FCSTD DOCUMENT  (FreeCAD 0.20R29177 (Git))
Label: Tail_Assembly
License: All rights reserved
LicenseURL: http://en.wikipedia.org/wiki/All_rights_reserved
objects: App::Link×2, Spreadsheet::Sheet×1, App::Part×1
EXTERNAL_REF file=../Master_of_Puppets.FCStd obj=HighEndStop
EXTERNAL_REF file=Hinge/Inner/Tail_Hinge_Inner.FCStd obj=Part001
EXTERNAL_REF file=Tail.FCStd obj=Part

FEATURE [Spreadsheet::Sheet] Spreadsheet
  cells = A1=Inputs; A2=TailAssemblyPlacement; B2(TailAssemblyPlacement)==Master_of_Puppets#HighEndStop.TailAssemblyPlacement
FEATURE [App::Link] Link  label="Hinge_Inner"
  LinkedObject = -> <external Hinge/Inner/Tail_Hinge_Inner.FCStd>#Part001
FEATURE [App::Link] Link001  label="Tail"
  LinkTransform = true
  LinkedObject = -> <external Tail.FCStd>#Part
FEATURE [App::Part] Part  label="Tail_Assembly"
  Group = -> [Link,Link001]
  Origin = -> Origin
  Placement = pos=(-8.64666,-12.3487,0) rot=(0,0,-1;2.18166rad)
  expr: Placement = Spreadsheet.TailAssemblyPlacement

RESOLVED EXTERNAL PARTS (link-assembly join: the EXTERNAL_REF files above that resolve inside this repo's crawl, each included once):
---- part ../Master_of_Puppets.FCStd = doc fcstd_6404554055c4 (61625 chars; too large to inline — full recipe in that document) ----
---- part Hinge/Inner/Tail_Hinge_Inner.FCStd = doc fcstd_5a32ac608b16 ----
FCSTD DOCUMENT  (FreeCAD 1.0R39109 (Git))
Label: Tail_Hinge_Inner
License: All rights reserved
LicenseURL: http://en.wikipedia.org/wiki/All_rights_reserved
objects: App::Link×3, Spreadsheet::Sheet×1, App::Part×1
EXTERNAL_REF file=Tail_Hinge_Inner_Pipe.FCStd obj=Tube
EXTERNAL_REF file=../../../Master_of_Puppets.FCStd obj=Spreadsheet
EXTERNAL_REF file=../../../Master_of_Puppets.FCStd obj=Tail
EXTERNAL_REF file=../Junction/Tail_Hinge_Junction.FCStd obj=Part
EXTERNAL_REF file=Tail_Hinge_Inner_Pipe_Cover.FCStd obj=Cylinder

FEATURE [App::Link] Link  label="Pipe"
  LinkPlacement = pos=(31.9025,0,-7.21663) rot=(0,1,0;0.349066rad)
  LinkedObject = -> <external Tail_Hinge_Inner_Pipe.FCStd>#Tube
  Placement = pos=(31.9025,0,-7.21663) rot=(0,1,0;0.349066rad)
  expr: .LinkPlacement.Base.x = Spreadsheet.TailHingePipeX
  expr: .LinkPlacement.Base.z = Spreadsheet.TailHingePipeZ
  expr: Placement = Spreadsheet.HingeInnerPipePlacement
FEATURE [Spreadsheet::Sheet] Spreadsheet
  cells = A1='Inputs; A2='VerticalPlaneAngle; B2(VerticalPlaneAngle)==Master_of_Puppets#Spreadsheet.VerticalPlaneAngle; A3='HingeInnerPipeRadius; B3(HingeInnerPipeRadius)==Master_of_Puppets#Tail.HingeInnerPipeRadius; A4='FlatMetalThickness; B4(FlatMetalThickness)==Master_of_Puppets#Spreadsheet.FlatMetalThickness; A5='Height; B5(Height)==Master_of_Puppets#Tail.TailHingeJunctionHeight; A6='Chamfer; B6(Chamfer)==Master_of_Puppets#Tail.TailHingeJunctionChamfer; A7='FullWidth; B7(FullWidth)==Master_of_Puppets#Tail.TailHingeJunctionFullWidth; A8='TailHingePipeZ; B8(TailHingePipeZ)==Master_of_Puppets#Tail.TailHingePipeZ; A9='TailHingePipeX; B9(TailHingePipeX)==Master_of_Puppets#Tail.TailHingePipeX; A10='HingeInnerPipeLength; B10(HingeInnerPipeLength)==Master_of_Puppets#Tail.HingeInnerPipeLength; A11='HingeInnerPipeDisplayCover; B11(HingeInnerPipeDisplayCover)==Master_of_Puppets#Tail.HingeInnerPipeDisplayCover; A12='Calculated; A13='TailHingeJunctionX; B13(TailHingeJunctionX)==-Chamfer; A14='HingeInnerPipePlacement; B14(HingeInnerPipePlacement)==placement(vector(TailHingePipeX; 0; TailHingePipeZ); vector(0; 1; 0); VerticalPlaneAngle); A15='HingeInnerPipeCoverPlacement; B15(HingeInnerPipeCoverPlacement)==HingeInnerPipePlacement * placement(vector(0; 0; HingeInnerPipeLength); vector(0; 0; 1); 0)
FEATURE [App::Link] Link005  label="Junction"
  LinkPlacement = pos=(-12.075,0,0) rot=(0,0,1;0rad)
  LinkedObject = -> <external ../Junction/Tail_Hinge_Junction.FCStd>#Part
  Placement = pos=(-12.075,0,0) rot=(0,0,1;0rad)
  expr: .Placement.Base.x = Spreadsheet.TailHingeJunctionX
FEATURE [App::Link] Link006  label="Tail_Hinge_Inner_Pipe_Cover"
  LinkPlacement = pos=(93.2691,0,161.387) rot=(0,1,0;0.349066rad)
  LinkedObject = -> <external Tail_Hinge_Inner_Pipe_Cover.FCStd>#Cylinder
  Placement = pos=(93.2691,0,161.387) rot=(0,1,0;0.349066rad)
  expr: Placement = Spreadsheet.HingeInnerPipeCoverPlacement
  expr: Visibility = Spreadsheet.HingeInnerPipeDisplayCover
FEATURE [App::Part] Part001  label="Tail_Hinge_Inner"
  Group = -> [Link,Link005,Link006]
  Origin = -> Origin001
---- part Tail.FCStd = doc fcstd_b48a271e5d2f ----
FCSTD DOCUMENT  (FreeCAD 0.20R29177 (Git))
Label: Tail
License: All rights reserved
LicenseURL: http://en.wikipedia.org/wiki/All_rights_reserved
objects: App::Link×2, Spreadsheet::Sheet×1, App::Part×1
EXTERNAL_REF file=../Master_of_Puppets.FCStd obj=HighEndStop
EXTERNAL_REF file=../Master_of_Puppets.FCStd obj=Tail
EXTERNAL_REF file=Tail_Assembly_BoomVane.FCStd obj=Part001
EXTERNAL_REF file=Hinge/Outer/Tail_Hinge_Outer.FCStd obj=Part

FEATURE [Spreadsheet::Sheet] Spreadsheet
  cells = A1=Inputs; A2=TailPlacement (TailBoomVaneAssembly); B2(TailPlacement)==Master_of_Puppets#HighEndStop.TailPlacement; A3=OuterTailHingePlacement; B3(OuterTailHingePlacement)==Master_of_Puppets#Tail.OuterTailHingePlacement; A4=FurlAxis; B4(FurlAxis)==Master_of_Puppets#HighEndStop.FurlAxis
FEATURE [App::Link] Link  label="Assembly_BoomVane"
  LinkPlacement = pos=(126.484,5.6656,173.663) rot=(0,0,1;0.261799rad)
  LinkTransform = true
  LinkedObject = -> <external Tail_Assembly_BoomVane.FCStd>#Part001
  Placement = pos=(126.484,5.6656,173.663) rot=(0,0,1;0.261799rad)
  expr: LinkPlacement = Spreadsheet.TailPlacement
FEATURE [App::Link] Link001  label="Hinge_Outer"
  LinkPlacement = pos=(76.7329,0,98.7939) rot=(0,1,0;0.349066rad)
  LinkedObject = -> <external Hinge/Outer/Tail_Hinge_Outer.FCStd>#Part
  Placement = pos=(76.7329,0,98.7939) rot=(0,1,0;0.349066rad)
  expr: LinkPlacement = Spreadsheet.OuterTailHingePlacement
FEATURE [App::Part] Part  label="Tail"
  Group = -> [Link001,Link]
  Origin = -> Origin
  expr: .Placement.Rotation.Axis = Spreadsheet.FurlAxis
